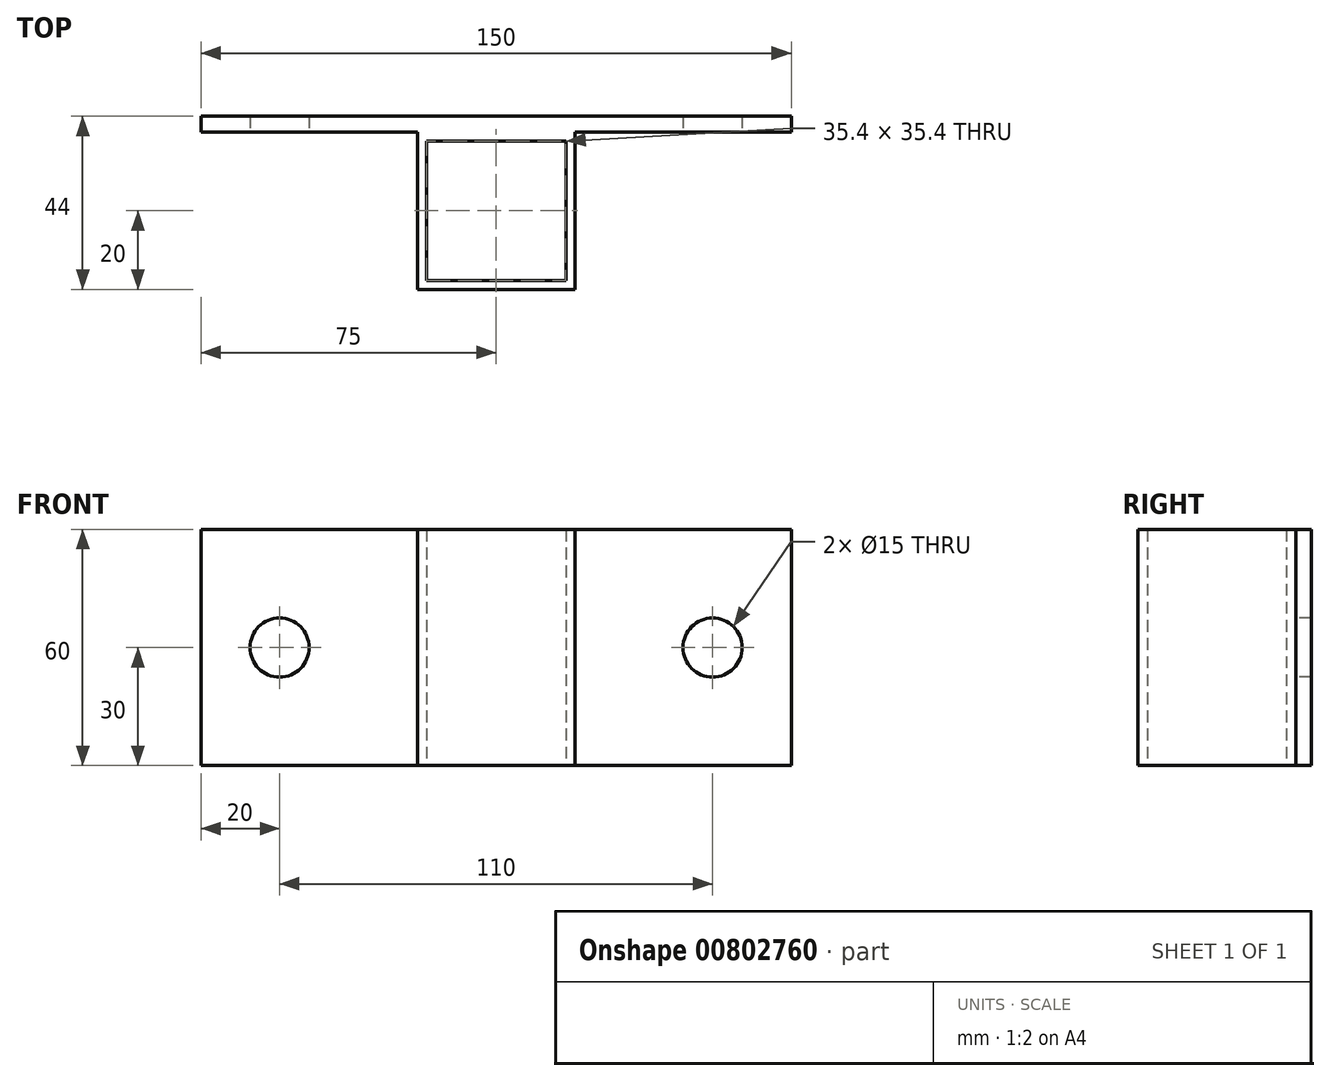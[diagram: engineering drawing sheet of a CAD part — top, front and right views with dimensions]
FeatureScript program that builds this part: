
annotation { "Feature Type Name" : "Feature", "Feature Type Description" : "" }
export const myFeature = defineFeature(function(context is Context, id is Id, definition is map)
    precondition{}
    {
        {
            var Q0;
            Q0=qCreatedBy(makeId("Top.planeOp"),FACE);
            var sketch = newSketch(context, id + "F0", { "sketchPlane" : qUnion([Q0])});
            skLineSegment(sketch, "E0.bottom", {"start": v(20, 20) * mm, "end": v(-20, 20) * mm});
            skLineSegment(sketch, "E0.top", {"start": v(20, -20) * mm, "end": v(-20, -20) * mm});
            skLineSegment(sketch, "E0.left", {"start": v(20, 20) * mm, "end": v(20, -20) * mm});
            skLineSegment(sketch, "E0.right", {"start": v(-20, 20) * mm, "end": v(-20, -20) * mm});
            skPoint(sketch, "E0.middle", {"position": v(0, 0) * mm});
            skLineSegment(sketch, "E1.bottom", {"start": v(-75, 20) * mm, "end": v(75, 20) * mm});
            skLineSegment(sketch, "E1.top", {"start": v(-75, 24) * mm, "end": v(75, 24) * mm});
            skLineSegment(sketch, "E1.left", {"start": v(-75, 20) * mm, "end": v(-75, 24) * mm});
            skLineSegment(sketch, "E1.right", {"start": v(75, 20) * mm, "end": v(75, 24) * mm});
            skLineSegment(sketch, "E2.bottom", {"start": v(17.7, 17.7) * mm, "end": v(-17.7, 17.7) * mm});
            skLineSegment(sketch, "E2.top", {"start": v(17.7, -17.7) * mm, "end": v(-17.7, -17.7) * mm});
            skLineSegment(sketch, "E2.left", {"start": v(17.7, 17.7) * mm, "end": v(17.7, -17.7) * mm});
            skLineSegment(sketch, "E2.right", {"start": v(-17.7, 17.7) * mm, "end": v(-17.7, -17.7) * mm});
            skSolve(sketch);
        }
        {
            var Q0;
            Q0=makeQuery(id+"F0.imprint","IMPRINT",FACE,{"disambiguationData":[TD([[makeQuery(id+"F0.imprint","IMPRINT",EDGE,{"derivedFrom":sQuery(id+"F0.wireOp",EDGE,"E1.top")}),-1.0]])]});
            var Q1;
            Q1=makeQuery(id+"F0.imprint","IMPRINT",FACE,{"disambiguationData":[TD([[makeQuery(id+"F0.imprint","IMPRINT",EDGE,{"derivedFrom":sQuery(id+"F0.wireOp",EDGE,"E0.top")}),-1.0]])]});
            extrude(context, id + "F1", {"entities" : qUnion([Q0, Q1]), "depth" : 60 * mm, "offsetDistance" : 25 * mm});
        }
        {
            var Q0;
            Q0=makeQuery(id+"F1.opExtrude","SWEPT_FACE",FACE,{"disambiguationData":[OSD([sQuery(id+"F0.wireOp",EDGE,"E1.bottom")])]});
            var sketch = newSketch(context, id + "F2", { "sketchPlane" : qUnion([Q0])});
            skCircle(sketch, "E3", {"center": v(-55, 30) * mm, "radius": 7.5 * mm});
            skCircle(sketch, "E4", {"center": v(55, 30) * mm, "radius": 7.5 * mm});
            skSolve(sketch);
        }
        {
            var Q0;
            Q0=makeQuery(id+"F2.imprint","IMPRINT",FACE,{"disambiguationData":[TD([[makeQuery(id+"F2.imprint","IMPRINT",EDGE,{"derivedFrom":sQuery(id+"F2.wireOp",EDGE,"E3")}),1.0]])]});
            var Q1;
            Q1=makeQuery(id+"F2.imprint","IMPRINT",FACE,{"disambiguationData":[TD([[makeQuery(id+"F2.imprint","IMPRINT",EDGE,{"derivedFrom":sQuery(id+"F2.wireOp",EDGE,"E4")}),1.0]])]});
            extrude(context, id + "F3", {"entities" : qUnion([Q0, Q1]), "operationType" : NewBodyOperationType.REMOVE, "endBound" : BoundingType.THROUGH_ALL, "oppositeDirection" : true, "depth" : 25 * mm, "offsetDistance" : 25 * mm});
        }
    });
